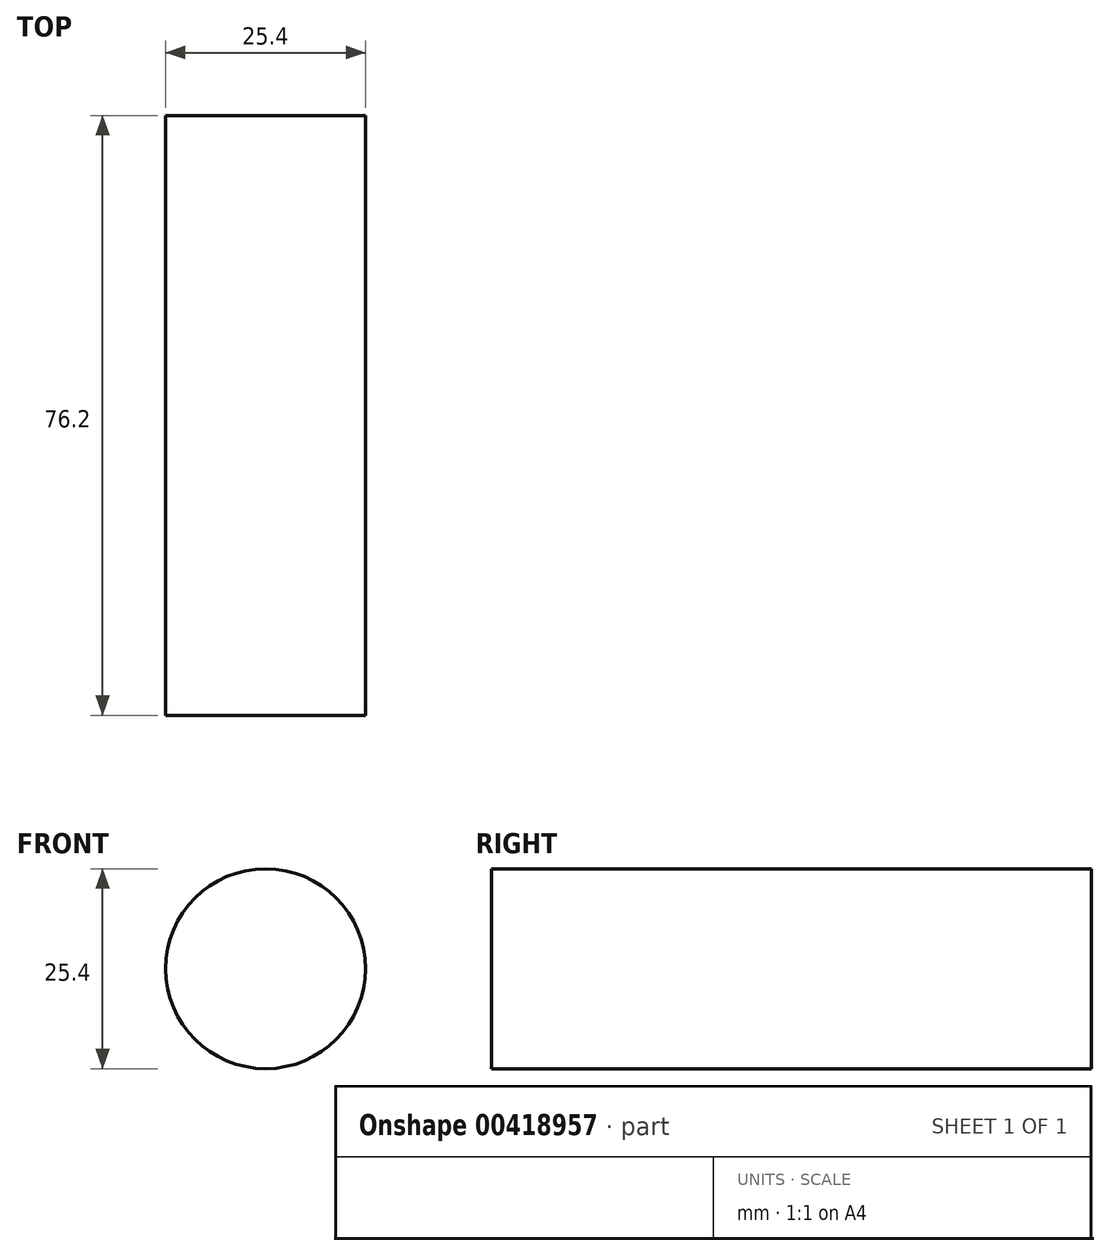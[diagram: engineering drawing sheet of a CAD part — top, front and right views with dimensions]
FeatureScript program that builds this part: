
annotation { "Feature Type Name" : "Feature", "Feature Type Description" : "" }
export const myFeature = defineFeature(function(context is Context, id is Id, definition is map)
    precondition{}
    {
        {
            var Q0;
            Q0=qCreatedBy(makeId("Front.planeOp"),FACE);
            var sketch = newSketch(context, id + "F0", { "sketchPlane" : qUnion([Q0])});
            skCircle(sketch, "E0", {"center": v(-25.4, 20.62) * mm, "radius": 12.7 * mm});
            skSolve(sketch);
        }
        {
            var Q0;
            Q0 = qSketchRegion(id + "F0", true);
            extrude(context, id + "F1", {"entities" : qUnion([Q0]), "depth" : 76.2 * mm});
        }
    });
